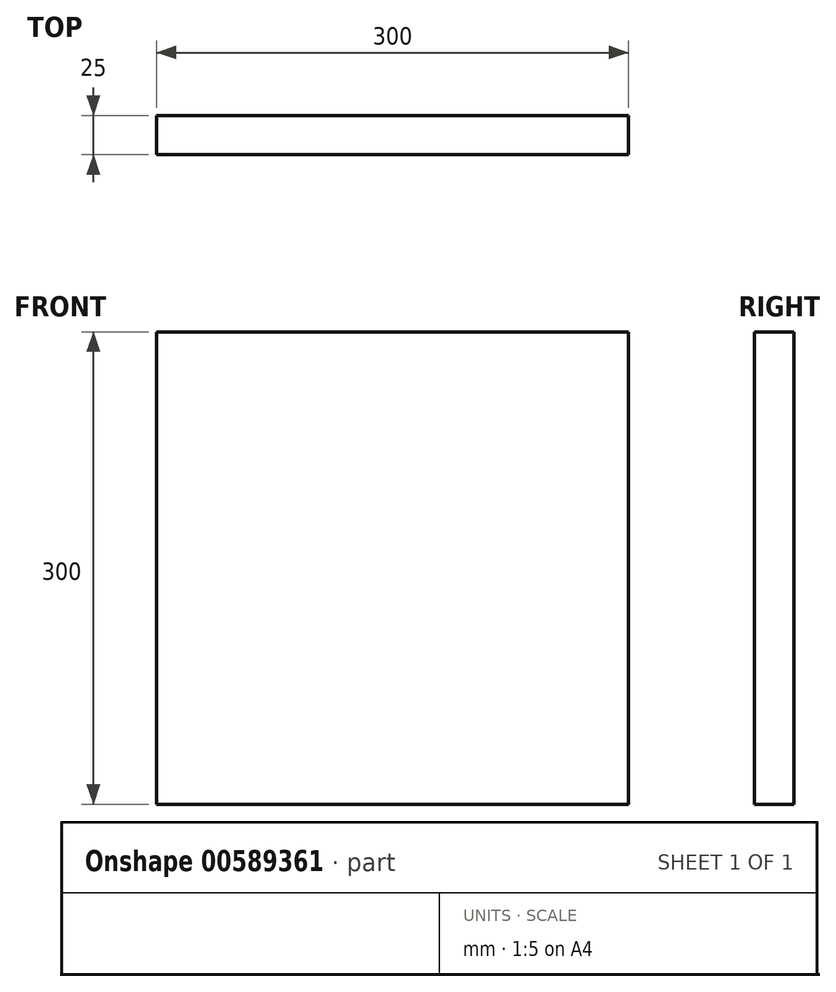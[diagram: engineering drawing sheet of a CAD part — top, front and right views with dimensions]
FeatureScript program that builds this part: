
annotation { "Feature Type Name" : "Feature", "Feature Type Description" : "" }
export const myFeature = defineFeature(function(context is Context, id is Id, definition is map)
    precondition{}
    {
        {
            var Q0;
            Q0=qCreatedBy(makeId("Front.planeOp"),FACE);
            var sketch = newSketch(context, id + "F0", { "sketchPlane" : qUnion([Q0])});
            skLineSegment(sketch, "E0.bottom", {"start": v(-154.62, 175.98) * mm, "end": v(145.38, 175.98) * mm});
            skLineSegment(sketch, "E0.top", {"start": v(-154.62, -124.02) * mm, "end": v(145.38, -124.02) * mm});
            skLineSegment(sketch, "E0.left", {"start": v(-154.62, 175.98) * mm, "end": v(-154.62, -124.02) * mm});
            skLineSegment(sketch, "E0.right", {"start": v(145.38, 175.98) * mm, "end": v(145.38, -124.02) * mm});
            skSolve(sketch);
        }
        {
            var Q0;
            Q0=makeQuery(id+"F0.imprint","IMPRINT",FACE,{"disambiguationData":[TD([[makeQuery(id+"F0.imprint","IMPRINT",EDGE,{"derivedFrom":sQuery(id+"F0.wireOp",EDGE,"E0.bottom")}),-1.0]])]});
            extrude(context, id + "F1", {"entities" : qUnion([Q0]), "depth" : 25 * mm, "offsetDistance" : 25 * mm});
        }
    });
